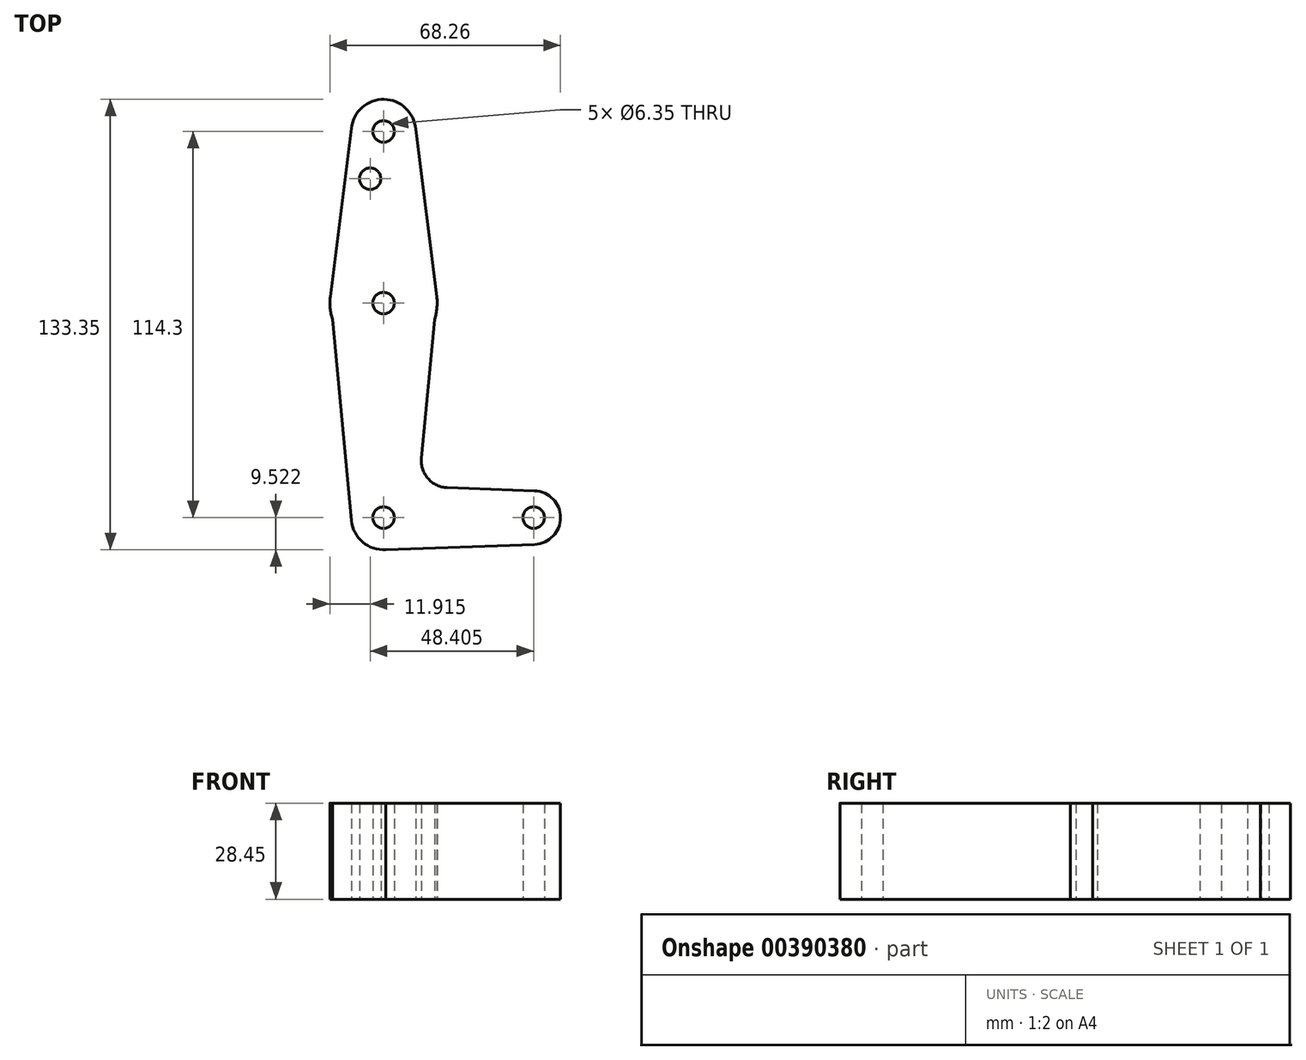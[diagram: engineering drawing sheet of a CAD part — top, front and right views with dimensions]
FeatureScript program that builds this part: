
annotation { "Feature Type Name" : "Feature", "Feature Type Description" : "" }
export const myFeature = defineFeature(function(context is Context, id is Id, definition is map)
    precondition{}
    {
        {
            var Q0;
            Q0=qCreatedBy(makeId("Top.planeOp"),FACE);
            var sketch = newSketch(context, id + "F0", { "sketchPlane" : qUnion([Q0])});
            skCircle(sketch, "E0", {"center": v(0, 48.94) * mm, "radius": 9.53 * mm});
            skCircle(sketch, "E1", {"center": v(0, -1.86) * mm, "radius": 15.88 * mm});
            skCircle(sketch, "E2", {"center": v(0, -65.36) * mm, "radius": 9.53 * mm});
            skCircle(sketch, "E3", {"center": v(44.45, -65.36) * mm, "radius": 7.94 * mm});
            skLineSegment(sketch, "E4", {"start": v(-9.4, 50.43) * mm, "end": v(-15.77, 0) * mm});
            skLineSegment(sketch, "E5", {"start": v(9.36, 50.7) * mm, "end": v(15.77, 0) * mm});
            skLineSegment(sketch, "E6", {"start": v(15.77, 0) * mm, "end": v(11.23, -47.8) * mm});
            skLineSegment(sketch, "E7", {"start": v(-15.77, 0) * mm, "end": v(-9.48, -66.26) * mm});
            skLineSegment(sketch, "E8", {"start": v(18.86, -56.5) * mm, "end": v(44.73, -57.43) * mm});
            skLineSegment(sketch, "E9", {"start": v(0, -74.88) * mm, "end": v(44.73, -73.3) * mm});
            skPoint(sketch, "E10.newPointB", {"position": v(0, -55.83) * mm});
            skArc(sketch, "E10.filletArc", {"start": v(11.23, -47.8) * mm, "mid": v(13.17, -53.8) * mm, "end": v(18.86, -56.5) * mm});
            skCircle(sketch, "E11", {"center": v(0, 48.94) * mm, "radius": 3.18 * mm});
            skCircle(sketch, "E12", {"center": v(0, -1.86) * mm, "radius": 3.18 * mm});
            skCircle(sketch, "E13", {"center": v(0, -65.36) * mm, "radius": 3.18 * mm});
            skCircle(sketch, "E14", {"center": v(44.45, -65.36) * mm, "radius": 3.18 * mm});
            skCircle(sketch, "E15", {"center": v(-3.95, 34.94) * mm, "radius": 3.18 * mm});
            skSolve(sketch);
        }
        {
            var Q0;
            Q0 = qSketchRegion(id + "F0", true);
            extrude(context, id + "F1", {"entities" : qUnion([Q0]), "depth" : 3.05 * mm});
        }
        {
            var Q0;
            Q0=makeQuery(id+"F1.opExtrude","CAP_FACE",FACE,{"disambiguationData":[OSD([sQuery(id+"F0.wireOp",EDGE,"E0"),sQuery(id+"F0.wireOp",EDGE,"E1"),sQuery(id+"F0.wireOp",EDGE,"E2"),sQuery(id+"F0.wireOp",EDGE,"E3"),sQuery(id+"F0.wireOp",EDGE,"E4"),sQuery(id+"F0.wireOp",EDGE,"E5"),sQuery(id+"F0.wireOp",EDGE,"E6"),sQuery(id+"F0.wireOp",EDGE,"E7"),sQuery(id+"F0.wireOp",EDGE,"E8"),sQuery(id+"F0.wireOp",EDGE,"E9"),sQuery(id+"F0.wireOp",EDGE,"E10.filletArc"),sQuery(id+"F0.wireOp",EDGE,"E11"),sQuery(id+"F0.wireOp",EDGE,"E12"),sQuery(id+"F0.wireOp",EDGE,"E13"),sQuery(id+"F0.wireOp",EDGE,"E14"),sQuery(id+"F0.wireOp",EDGE,"E15")])],"isStart":false});
            extrude(context, id + "F2", {"entities" : qUnion([Q0]), "operationType" : NewBodyOperationType.ADD, "depth" : 25.4 * mm});
        }
    });
